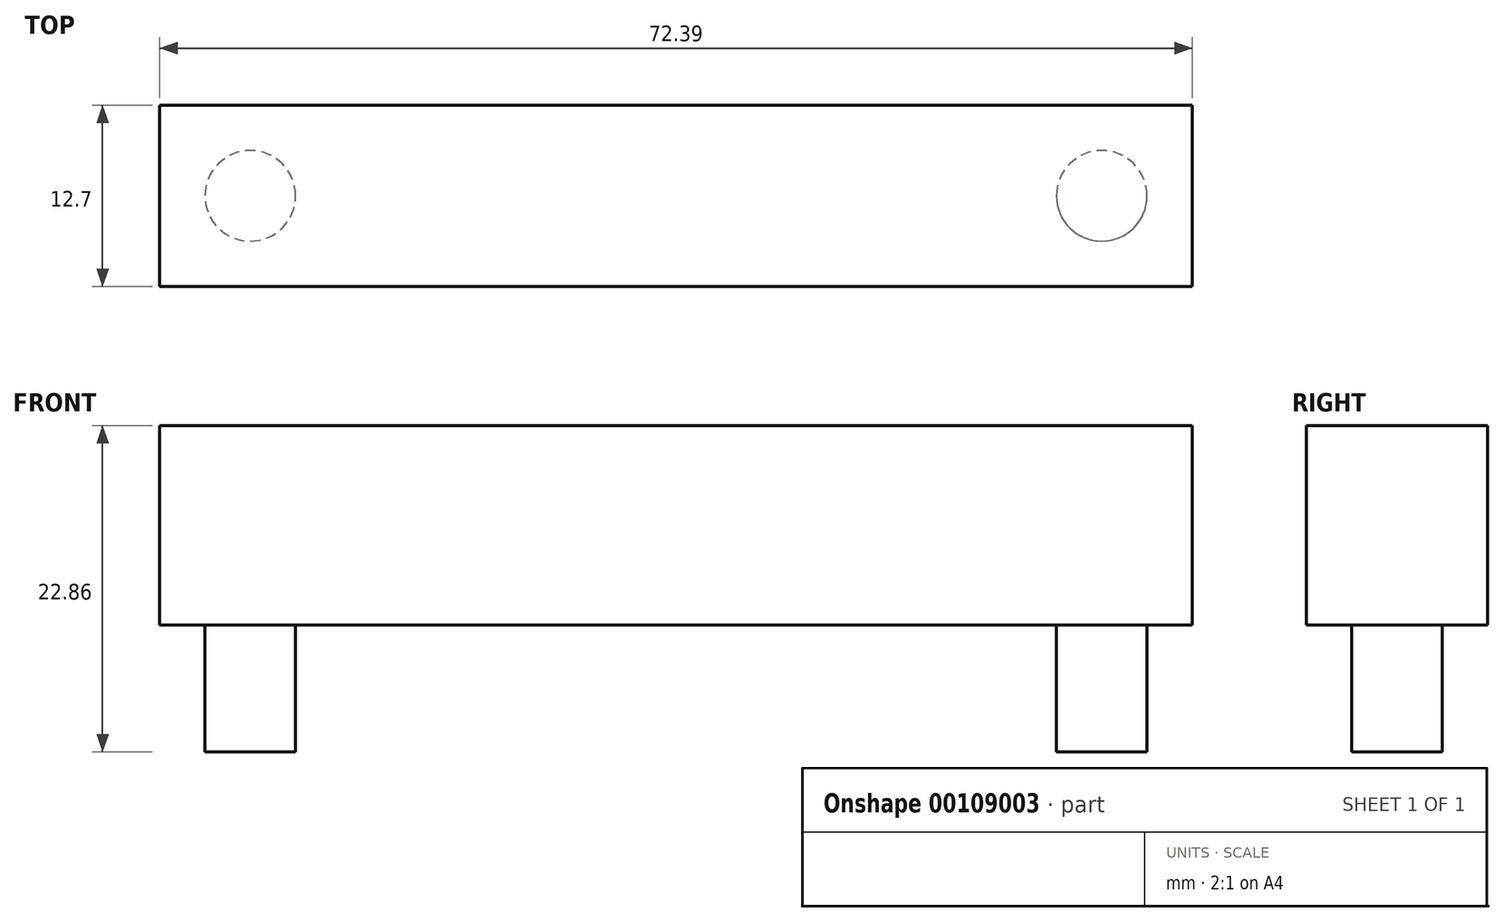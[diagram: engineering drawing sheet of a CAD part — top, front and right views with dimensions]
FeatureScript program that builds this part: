
annotation { "Feature Type Name" : "Feature", "Feature Type Description" : "" }
export const myFeature = defineFeature(function(context is Context, id is Id, definition is map)
    precondition{}
    {
        {
            var Q0;
            Q0=qCreatedBy(makeId("Top.planeOp"),FACE);
            var sketch = newSketch(context, id + "F0", { "sketchPlane" : qUnion([Q0])});
            skLineSegment(sketch, "E0", {"start": v(0, 0) * mm, "end": v(0, 12.7) * mm});
            skLineSegment(sketch, "E1", {"start": v(0, 12.7) * mm, "end": v(47, 12.7) * mm});
            skLineSegment(sketch, "E2", {"start": v(47, 12.7) * mm, "end": v(47, 0) * mm});
            skLineSegment(sketch, "E3", {"start": v(47, 0) * mm, "end": v(0, 0) * mm});
            skLineSegment(sketch, "E4", {"start": v(-25.4, 0) * mm, "end": v(-25.4, 12.7) * mm});
            skLineSegment(sketch, "E5", {"start": v(-25.4, 12.7) * mm, "end": v(0, 12.7) * mm});
            skLineSegment(sketch, "E6", {"start": v(-25.4, 0) * mm, "end": v(0, 0) * mm});
            skSolve(sketch);
        }
        {
            var Q0;
            Q0=makeQuery(id+"F0.imprint","IMPRINT",FACE,{"disambiguationData":[TD([[makeQuery(id+"F0.imprint","IMPRINT",EDGE,{"derivedFrom":sQuery(id+"F0.wireOp",EDGE,"E0")}),1.0]])]});
            var Q1;
            Q1=makeQuery(id+"F0.imprint","IMPRINT",FACE,{"disambiguationData":[TD([[makeQuery(id+"F0.imprint","IMPRINT",EDGE,{"derivedFrom":sQuery(id+"F0.wireOp",EDGE,"E0")}),-1.0]])]});
            extrude(context, id + "F1", {"entities" : qUnion([Q0, Q1]), "depth" : 7.62 * mm});
        }
        {
            var Q0;
            Q0=makeQuery(id+"F1.opExtrude","CAP_FACE",FACE,{"disambiguationData":[OSD([sQuery(id+"F0.wireOp",EDGE,"E1"),sQuery(id+"F0.wireOp",EDGE,"E2"),sQuery(id+"F0.wireOp",EDGE,"E3"),sQuery(id+"F0.wireOp",EDGE,"E4"),sQuery(id+"F0.wireOp",EDGE,"E5"),sQuery(id+"F0.wireOp",EDGE,"E6")])],"isStart":true});
            var sketch = newSketch(context, id + "F2", { "sketchPlane" : qUnion([Q0])});
            skLineSegment(sketch, "E7", {"start": v(-25.4, -6.35) * mm, "end": v(-19.05, -6.35) * mm});
            skCircle(sketch, "E8", {"center": v(-19.05, -6.35) * mm, "radius": 3.18 * mm});
            skLineSegment(sketch, "E9", {"start": v(47, -6.35) * mm, "end": v(40.64, -6.35) * mm});
            skCircle(sketch, "E10", {"center": v(40.64, -6.35) * mm, "radius": 3.18 * mm});
            skLineSegment(sketch, "E11", {"start": v(-19.05, -6.35) * mm, "end": v(-12.7, -6.35) * mm});
            skLineSegment(sketch, "E12", {"start": v(-12.7, -6.35) * mm, "end": v(-12.7, 0) * mm});
            skLineSegment(sketch, "E13", {"start": v(-12.7, -6.35) * mm, "end": v(-12.7, -12.7) * mm});
            skLineSegment(sketch, "E14", {"start": v(40.64, -6.35) * mm, "end": v(34.3, -6.35) * mm});
            skLineSegment(sketch, "E15", {"start": v(34.12, -6.36) * mm, "end": v(34.12, -12.7) * mm});
            skLineSegment(sketch, "E16", {"start": v(34.12, -12.7) * mm, "end": v(34.12, 0) * mm});
            skSolve(sketch);
        }
        {
            var Q0;
            Q0=makeQuery(id+"F2.imprint","IMPRINT",FACE,{"disambiguationData":[TD([[makeQuery(id+"F2.imprint","IMPRINT",EDGE,{"derivedFrom":sQuery(id+"F2.wireOp",EDGE,"E8")}),1.0]])]});
            var Q1;
            Q1=makeQuery(id+"F2.imprint","IMPRINT",FACE,{"disambiguationData":[TD([[makeQuery(id+"F2.imprint","IMPRINT",EDGE,{"derivedFrom":sQuery(id+"F2.wireOp",EDGE,"E10")}),1.0]])]});
            extrude(context, id + "F3", {"entities" : qUnion([Q0, Q1]), "operationType" : NewBodyOperationType.ADD, "depth" : 8.9 * mm});
        }
        {
            var Q0;
            Q0=makeQuery(id+"F1.opExtrude","CAP_FACE",FACE,{"disambiguationData":[OSD([sQuery(id+"F0.wireOp",EDGE,"E1"),sQuery(id+"F0.wireOp",EDGE,"E2"),sQuery(id+"F0.wireOp",EDGE,"E3"),sQuery(id+"F0.wireOp",EDGE,"E4"),sQuery(id+"F0.wireOp",EDGE,"E5"),sQuery(id+"F0.wireOp",EDGE,"E6")])],"isStart":false});
            extrude(context, id + "F4", {"entities" : qUnion([Q0]), "operationType" : NewBodyOperationType.ADD, "depth" : 6.35 * mm});
        }
    });
